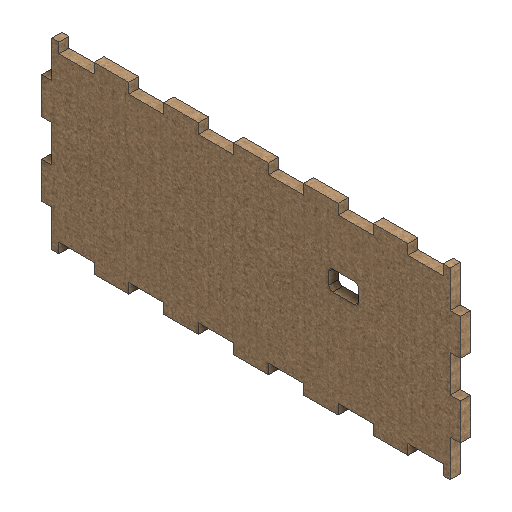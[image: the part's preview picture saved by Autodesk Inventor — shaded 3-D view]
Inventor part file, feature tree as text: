
AUTODESK INVENTOR PART (.ipt)
format: ipt  version: 2025.2 (Build 292293000, 293)  size: 389,120 bytes
history: native  units: mm
features: sketch x4, extrude x3, fillet x1
ambient origin geometry x8: Origin, YZ Plane, XZ Plane, XY Plane, X Axis, Y Axis, Z Axis, Center Point
bodies: Solid1 (feature_tree)
feature tree (8):
  extrude  "Extrusion1"  Depth=92.0mm
  extrude  "Extrusion2"  Depth=5.0mm
  fillet  "Fillet1"  Radius=55.6mm
  extrude  "Extrusion3"  Depth=10.0mm
  sketch  "Sketch1"  dims[d0=210.0mm d1=92.0mm]
  sketch  "Sketch2"  dims[d7=15.0mm d8=10.0mm]
  sketch  "Sketch3"  dims[d9=10.0mm d10=5.0mm d12=88.0mm d13=20.0mm d15=5.0mm d16=0.0mm d17=3.5mm d18=72.75mm d19=1.5mm d20=38.5mm d21=2.0mm d23=30.0mm d25=10.0mm d26=210.0mm d27=17.55mm d28=17.6mm d29=5.1mm d30=35.0mm d31=10.0mm d32=210.0mm d33=5.0mm d34=0.0mm d35=92.0mm d38=18.5mm]
  sketch  "Sketch Rectangular Pattern1"  dims[d2=5.0mm d3=0.0mm d4=1.6mm d5=55.6mm]
